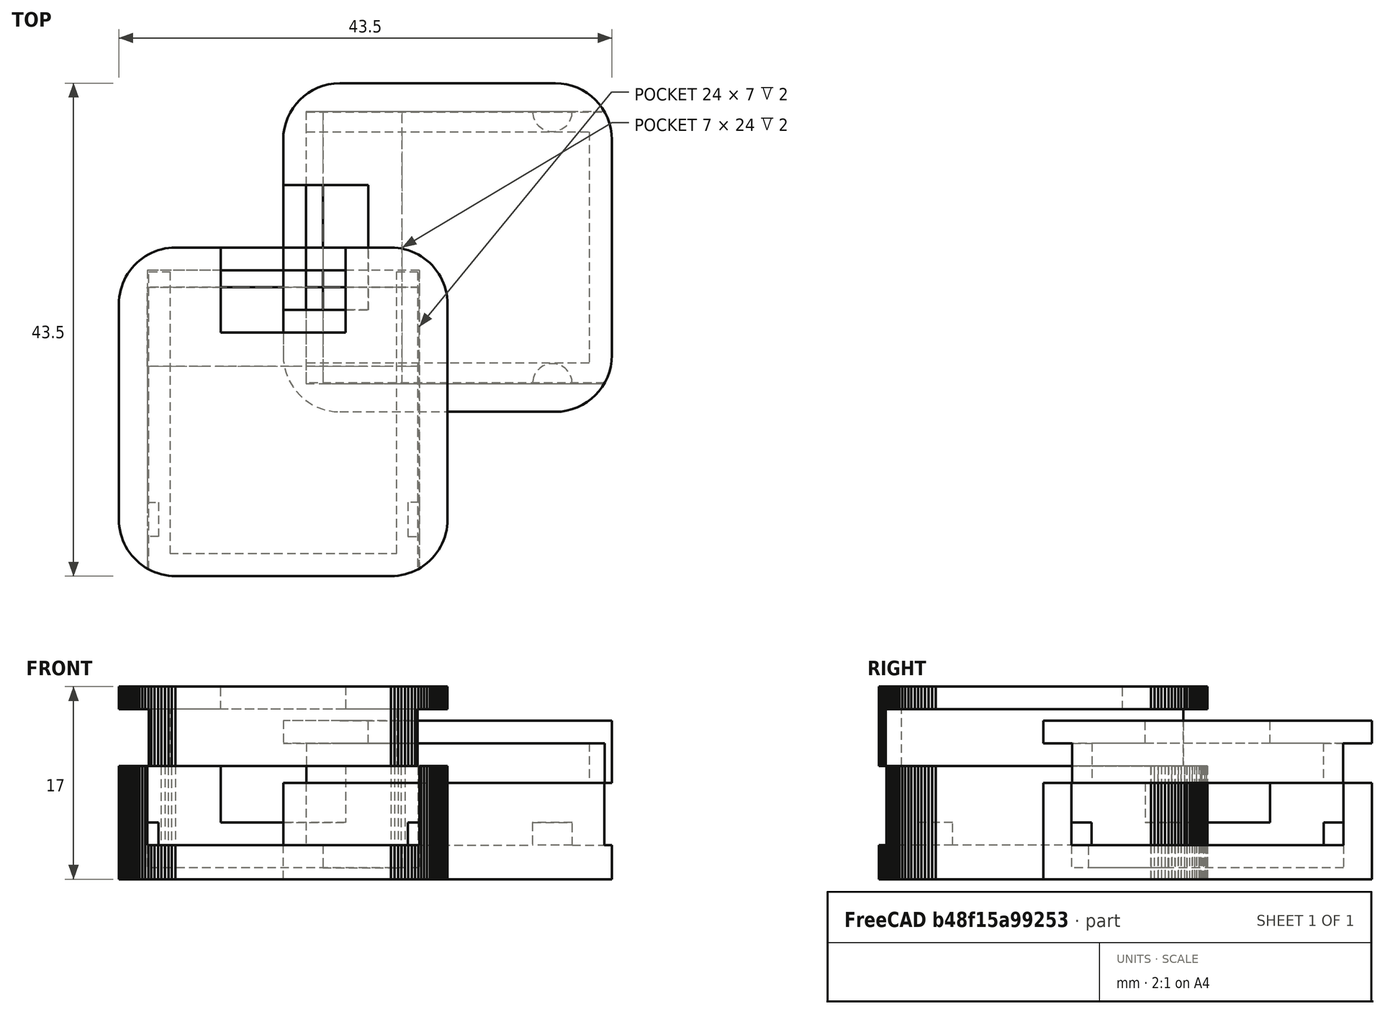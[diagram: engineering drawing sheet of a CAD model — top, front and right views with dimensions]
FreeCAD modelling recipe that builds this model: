
FCSTD DOCUMENT  (FreeCAD 1.0R39109 (Git))
Label: peepMoistureSensor
License: All rights reserved
LicenseURL: https://en.wikipedia.org/wiki/All_rights_reserved
objects: Sketcher::SketchObject×10, PartDesign::Pocket×6, PartDesign::Pad×4, Part::Feature×4, Mesh::Feature×2, Part::Refine×2, PartDesign::Body×2, Spreadsheet::Sheet×1
note: 58 computed .brp shape members not serialized (recipe doc carries the construction recipe); baked Part::Feature solids carry a one-line shape summary decoded from their .brp

FEATURE [Sketcher::SketchObject] Sketch
  ArcFitTolerance = 1e-06
  AttachmentSupport = -> [XY_Plane]
  FullyConstrained = true
  MakeInternals = false
  MapMode = 5
  expr: Constraints[10] = <<Parameters>>.baseHeight
  expr: Constraints[9] = <<Parameters>>.baseWidth
  sketch-geometry (4):
    g0: LineSegment StartX=0 StartY=0 StartZ=0 EndX=29 EndY=0 EndZ=0
    g1: LineSegment StartX=29 StartY=0 StartZ=0 EndX=29 EndY=29 EndZ=0
    g2: LineSegment StartX=29 StartY=29 StartZ=0 EndX=0 EndY=29 EndZ=0
    g3: LineSegment StartX=0 StartY=29 StartZ=0 EndX=0 EndY=0 EndZ=0
  constraints (11):
    c: Coincident(g0,g1)
    c: Coincident(g1,g2)
    c: Coincident(g2,g3)
    c: Coincident(g3,g0)
    c: Horizontal(g0)
    c: Horizontal(g2)
    c: Vertical(g1)
    c: Vertical(g3)
    c: Coincident(g0,g-1)
    c: DistanceX(g2,g2) = 29
    c: DistanceY(g1,g1) = 29
FEATURE [PartDesign::Pad] Pad
  Direction = (0,0,1)
  Length = 8.5
  Length2 = 10
  Profile = -> Sketch
  ReferenceAxis = -> Sketch [N_Axis]
  Refine = true
  Suppressed = false
  Type = 0
  expr: Length = <<Parameters>>.baseDepth
FEATURE [Spreadsheet::Sheet] Spreadsheet  label="Parameters"
  cells = B1='height; C1='width; D1='depth; E1='distance; F1='radius; A2='Base; B2(baseHeight)==29 mm; C2(baseWidth)==29 mm; D2(baseDepth)==wholePartDepth - frontDepth; A3='Cover; B3(coverHeight)==baseHeight; C3(coverWidth)==baseWidth; D3(coverDepth)==frontDepth + coverWallDepth; A4='Sensor; B4(sensorHeight)==24 mm; C4(sensorWidth)==27 mm; D4(sensorDepth)==2 mm; A5='Sensor pins; B5(sensorPinsHeight)==sensorHeight; C5(sensorPinsWidth)==7 mm; D5(sensorPinsDepth)==2 mm; A6='Sensor Holder distance from sensor edge; E6(sensorHolderDistance)==3.5 mm; A7='Sensor Holder; D7(sensorHolderDepth)==sensorDepth; F7(sensorHolderRadius)==1.75 mm; A8='Connector; B8(connectorHeight)==11 mm; C8(connectorWidth)==7.5 mm; D8(connectorDepth)==baseDepth - backDepth - connectorDistance; E8(connectorDistance)==2 mm; A9='Back; D9(backDepth)==3 mm; A10='Front; D10(frontDepth)==2 mm; A11='Cover wall; B11(coverWallHeight)=1.75; C11(coverWallWidth)==2 mm; D11(coverWallDepth)==baseDepth - backDepth - sensorDepth; A12='Pins distance from sensor connector edge; E12(pinsDistance)==1.5 mm; A13='Whole part decor round radius; F13(decorRoundRadius)==5 mm; A16='Thickness; A17='Whole part; D17(wholePartDepth)==10.5 mm; A18='Space between; D18(space)==0.05 mm
FEATURE [Mesh::Feature] Capacitive_Soil_Moisture_Sensor_v1_2_Lower  label="Capacitive_Soil_Moisture_Sensor_v1.2_Lower"
FEATURE [Part::Feature] Capacitive_Soil_Moisture_Sensor_v1_2_Lower001
  shape: bbox 29 x 29 x 10 mm, 492 faces, 0 solids (baked)
FEATURE [Part::Feature] Capacitive_Soil_Moisture_Sensor_v1_2_Lower001_solid  label="Capacitive_Soil_Moisture_Sensor_v1_2_Lower001 (Solid)"
  shape: bbox 29 x 29 x 10 mm, 492 faces (baked)
FEATURE [Part::Refine] Capacitive_Soil_Moisture_Sensor_v1_2_Lower001_solid001  label="Capacitive_Soil_Moisture_Sensor_v1_2_Lower001 (Solid)001"
  Source = -> Capacitive_Soil_Moisture_Sensor_v1_2_Lower001_solid
FEATURE [Sketcher::SketchObject] Sketch001
  ArcFitTolerance = 1e-06
  AttachmentSupport = -> [Pad]
  ExternalGeometry = -> [Pad]
  FullyConstrained = true
  MakeInternals = false
  MapMode = 5
  Placement = pos=(0,0,8.5) rot=(0,0,1;0rad)
  expr: Constraints[10] = <<Parameters>>.sensorWidth
  expr: Constraints[9] = <<Parameters>>.sensorHeight
  sketch-geometry (5):
    g0: GeomPoint X=29 Y=14.5 Z=0
    g1: LineSegment StartX=29 StartY=26.5 StartZ=0 EndX=2 EndY=26.5 EndZ=0
    g2: LineSegment StartX=2 StartY=26.5 StartZ=0 EndX=2 EndY=2.5 EndZ=0
    g3: LineSegment StartX=2 StartY=2.5 StartZ=0 EndX=29 EndY=2.5 EndZ=0
    g4: LineSegment StartX=29 StartY=2.5 StartZ=0 EndX=29 EndY=26.5 EndZ=0
  constraints (12):
    c: Coincident(g1,g2)
    c: Coincident(g2,g3)
    c: Coincident(g3,g4)
    c: Coincident(g4,g1)
    c: Horizontal(g1)
    c: Horizontal(g3)
    c: Vertical(g2)
    c: Vertical(g4)
    c: Symmetric(g1,g3,g0)
    c: DistanceY(g4,g4) = 24
    c: DistanceX(g1,g1) = 27
    c: Symmetric(g-4,g-6,g0)
FEATURE [PartDesign::Pocket] Pocket
  BaseFeature = -> Pad
  Direction = (0,0,-1)
  Length = 5.5
  Length2 = 5
  Profile = -> Sketch001
  ReferenceAxis = -> Sketch001 [N_Axis]
  Refine = true
  Suppressed = false
  Type = 0
  expr: Length = <<Parameters>>.baseDepth - <<Parameters>>.backDepth
FEATURE [Sketcher::SketchObject] Sketch002
  ArcFitTolerance = 1e-06
  AttachmentSupport = -> [Pocket]
  ExternalGeometry = -> [Pocket]
  FullyConstrained = true
  MakeInternals = false
  MapMode = 5
  Placement = pos=(0,0,3) rot=(0,0,1;0rad)
  expr: Constraints[10] = <<Parameters>>.pinsDistance
  expr: Constraints[11] = <<Parameters>>.sensorPinsWidth
  sketch-geometry (4):
    g0: LineSegment StartX=3.5 StartY=2.5 StartZ=0 EndX=10.5 EndY=2.5 EndZ=0
    g1: LineSegment StartX=10.5 StartY=2.5 StartZ=0 EndX=10.5 EndY=26.5 EndZ=0
    g2: LineSegment StartX=10.5 StartY=26.5 StartZ=0 EndX=3.5 EndY=26.5 EndZ=0
    g3: LineSegment StartX=3.5 StartY=26.5 StartZ=0 EndX=3.5 EndY=2.5 EndZ=0
  constraints (12):
    c: Coincident(g0,g1)
    c: Coincident(g1,g2)
    c: Coincident(g2,g3)
    c: Coincident(g3,g0)
    c: Horizontal(g0)
    c: Horizontal(g2)
    c: Vertical(g1)
    c: Vertical(g3)
    c: PointOnObject(g0,g-5)
    c: PointOnObject(g1,g-4)
    c: DistanceX(g-4,g2) = 1.5
    c: DistanceX(g2,g2) = 7
FEATURE [PartDesign::Pocket] Pocket001
  BaseFeature = -> Pocket
  Direction = (0,0,-1)
  Length = 2
  Length2 = 5
  Profile = -> Sketch002
  ReferenceAxis = -> Sketch002 [N_Axis]
  Refine = true
  Suppressed = false
  Type = 0
  expr: Length = <<Parameters>>.sensorPinsDepth
FEATURE [Sketcher::SketchObject] Sketch003
  ArcFitTolerance = 1e-06
  AttachmentSupport = -> [Pocket001]
  ExternalGeometry = -> [Pocket001]
  FullyConstrained = true
  MakeInternals = false
  MapMode = 5
  Placement = pos=(0,0,3) rot=(0,0,1;0rad)
  expr: Constraints[1] = <<Parameters>>.sensorHolderRadius
  expr: Constraints[2] = <<Parameters>>.sensorHolderDistance + <<Parameters>>.sensorHolderRadius
  expr: Constraints[5] = <<Parameters>>.sensorHolderRadius
  expr: Constraints[7] = <<Parameters>>.sensorHolderDistance + <<Parameters>>.sensorHolderRadius
  sketch-geometry (3):
    g0: Circle CenterX=23.75 CenterY=2.5 CenterZ=0 NormalX=0 NormalY=0 NormalZ=1 AngleXU=0 Radius=1.75
    g1: LineSegment [constr] StartX=10.5 StartY=14.5 StartZ=0 EndX=29 EndY=14.5 EndZ=0
    g2: Circle CenterX=23.75 CenterY=26.5 CenterZ=0 NormalX=0 NormalY=0 NormalZ=1 AngleXU=0 Radius=1.75
  constraints (8):
    c: PointOnObject(g0,g-5)
    c: Radius(g0) = 1.75
    c: DistanceX(g0,g-5) = 5.25
    c: Symmetric(g-4,g-5,g1)
    c: Symmetric(g-6,g-6,g1)
    c: Radius(g2) = 1.75
    c: PointOnObject(g2,g-3)
    c: DistanceX(g2,g-4) = 5.25
FEATURE [PartDesign::Pad] Pad001
  BaseFeature = -> Pocket001
  Direction = (0,0,1)
  Length = 2
  Length2 = 10
  Profile = -> Sketch003
  ReferenceAxis = -> Sketch003 [N_Axis]
  Refine = true
  Suppressed = false
  Type = 0
  expr: Length = <<Parameters>>.sensorHolderDepth
FEATURE [Sketcher::SketchObject] Sketch004
  ArcFitTolerance = 1e-06
  AttachmentSupport = -> [Pad001]
  ExternalGeometry = -> [Pad001]
  FullyConstrained = true
  MakeInternals = false
  MapMode = 5
  Placement = pos=(0,0,8.5) rot=(0,0,1;0rad)
  expr: Constraints[11] = <<Parameters>>.connectorHeight
  sketch-geometry (5):
    g0: LineSegment StartX=0 StartY=20 StartZ=0 EndX=0 EndY=9 EndZ=0
    g1: LineSegment StartX=0 StartY=9 StartZ=0 EndX=2 EndY=9 EndZ=0
    g2: LineSegment StartX=2 StartY=9 StartZ=0 EndX=2 EndY=20 EndZ=0
    g3: LineSegment StartX=2 StartY=20 StartZ=0 EndX=0 EndY=20 EndZ=0
    g4: GeomPoint X=0 Y=14.5 Z=0
  constraints (12):
    c: Coincident(g0,g1)
    c: Coincident(g1,g2)
    c: Coincident(g2,g3)
    c: Coincident(g3,g0)
    c: Vertical(g0)
    c: Vertical(g2)
    c: Horizontal(g1)
    c: Horizontal(g3)
    c: PointOnObject(g1,g-4)
    c: Symmetric(g0,g0,g4)
    c: Symmetric(g-6,g-1,g4)
    c: DistanceY(g2,g2) = 11
FEATURE [PartDesign::Pocket] Pocket002
  BaseFeature = -> Pad001
  Direction = (0,0,-1)
  Length = 3.5
  Length2 = 5
  Profile = -> Sketch004
  ReferenceAxis = -> Sketch004 [N_Axis]
  Refine = true
  Suppressed = false
  Type = 0
  expr: Length = <<Parameters>>.connectorDepth
FEATURE [Sketcher::SketchObject] Sketch005
  ArcFitTolerance = 1e-06
  AttachmentSupport = -> [Pocket002]
  ExternalGeometry = -> [Pocket002]
  FullyConstrained = true
  MakeInternals = false
  MapMode = 5
  Placement = pos=(0,0,0) rot=(1,0,0;3.14159rad)
  expr: Constraints[1] = <<Parameters>>.decorRoundRadius
  expr: Constraints[22] = <<Parameters>>.decorRoundRadius
  expr: Constraints[37] = <<Parameters>>.decorRoundRadius
  expr: Constraints[38] = <<Parameters>>.decorRoundRadius
  expr: Constraints[8] = <<Parameters>>.decorRoundRadius
  sketch-geometry (17):
    g0: ArcOfCircle CenterX=5 CenterY=-5 CenterZ=0 NormalX=0 NormalY=0 NormalZ=1 AngleXU=0 Radius=5 StartAngle=1.5708 EndAngle=3.14159
    g1: GeomPoint [constr] X=3.9941e-12 Y=-2.31e-14 Z=0
    g2: LineSegment StartX=3.9941e-12 StartY=-2.31e-14 StartZ=0 EndX=3.9941e-12 EndY=-5 EndZ=0
    g3: LineSegment StartX=3.9941e-12 StartY=-2.31e-14 StartZ=0 EndX=5 EndY=-2.31e-14 EndZ=0
    g4: GeomPoint X=0 Y=-14.5 Z=0
    g5: GeomPoint X=14.5 Y=0 Z=0
    g6: LineSegment [constr] StartX=0 StartY=-14.5 StartZ=0 EndX=29 EndY=-14.5 EndZ=0
    g7: LineSegment [constr] StartX=14.5 StartY=0 StartZ=0 EndX=14.5 EndY=-29 EndZ=0
    g8: ArcOfCircle CenterX=5 CenterY=-24 CenterZ=0 NormalX=0 NormalY=0 NormalZ=1 AngleXU=0 Radius=5 StartAngle=3.14159 EndAngle=4.71239
    g9: LineSegment StartX=0 StartY=-29 StartZ=0 EndX=0 EndY=-24 EndZ=0
    g10: LineSegment StartX=0 StartY=-29 StartZ=0 EndX=5 EndY=-29 EndZ=0
    g11: ArcOfCircle CenterX=24 CenterY=-5 CenterZ=0 NormalX=0 NormalY=0 NormalZ=1 AngleXU=0 Radius=5 StartAngle=0 EndAngle=1.5708
    g12: LineSegment StartX=29 StartY=0 StartZ=0 EndX=24 EndY=0 EndZ=0
    g13: LineSegment StartX=29 StartY=0 StartZ=0 EndX=29 EndY=-5 EndZ=0
    g14: ArcOfCircle CenterX=24 CenterY=-24 CenterZ=0 NormalX=0 NormalY=0 NormalZ=1 AngleXU=0 Radius=5 StartAngle=4.71239 EndAngle=6.28319
    g15: LineSegment StartX=29 StartY=-29 StartZ=0 EndX=24 EndY=-29 EndZ=0
    g16: LineSegment StartX=29 StartY=-29 StartZ=0 EndX=29 EndY=-24 EndZ=0
  constraints (43):
    c: Coincident(g1,g-1)
    c: Radius(g0) = 5
    c: Coincident(g2,g1)
    c: Tangent(g2,g0) = -1.5708
    c: Vertical(g2)
    c: Coincident(g3,g1)
    c: Coincident(g3,g0)
    c: Horizontal(g3)
    c: DistanceX(g1,g0) = 5
    c: Symmetric(g-4,g1,g5)
    c: Symmetric(g-3,g1,g4)
    c: Coincident(g6,g4)
    c: PointOnObject(g6,g-6)
    c: Coincident(g7,g5)
    c: PointOnObject(g7,g-5)
    c: Horizontal(g6)
    c: Vertical(g7)
    c: Radius(g8) = 5
    c: Tangent(g9,g8) = 1.5708
    c: Vertical(g9)
    c: Coincident(g10,g8)
    c: Horizontal(g10)
    c: DistanceX(g10,g10) = 5
    c: PointOnObject(g8,g-5)
    c: PointOnObject(g8,g-3)
    c: Coincident(g9,g10)
    c: Radius(g11) = 5
    c: Tangent(g13,g11) = 1.5708
    c: Vertical(g13)
    c: Coincident(g12,g11)
    c: Horizontal(g12)
    c: Radius(g14) = 5
    c: Tangent(g16,g14) = -1.5708
    c: Vertical(g16)
    c: Coincident(g15,g14)
    c: Horizontal(g15)
    c: Coincident(g16,g15)
    c: DistanceX(g15,g15) = 5
    c: DistanceX(g12,g12) = 5
    c: PointOnObject(g14,g-5)
    c: PointOnObject(g14,g-6)
    c: Coincident(g-6,g13)
    c: Coincident(g12,g13)
FEATURE [PartDesign::Pocket] Pocket003
  BaseFeature = -> Pocket002
  Direction = (0,0,1)
  Length = 5
  Length2 = 5
  Profile = -> Sketch005
  ReferenceAxis = -> Sketch005 [N_Axis]
  Refine = true
  Suppressed = false
  Type = 1
FEATURE [PartDesign::Body] Body  label="Base"
  AllowCompound = false
  Group = -> [Sketch,Pad,Sketch001,Pocket,Sketch002,Pocket001,Sketch003,Pad001,Sketch004,Pocket002,Sketch005,Pocket003]
  Origin = -> Origin
  Tip = -> Pocket003
FEATURE [Sketcher::SketchObject] Sketch006
  ArcFitTolerance = 1e-06
  AttachmentSupport = -> [XY_Plane001]
  FullyConstrained = true
  MakeInternals = false
  MapMode = 5
  expr: Constraints[10] = <<Parameters>>.coverWidth
  expr: Constraints[11] = <<Parameters>>.coverHeight
  sketch-geometry (4):
    g0: LineSegment StartX=0 StartY=29 StartZ=0 EndX=0 EndY=0 EndZ=0
    g1: LineSegment StartX=0 StartY=0 StartZ=0 EndX=29 EndY=0 EndZ=0
    g2: LineSegment StartX=29 StartY=0 StartZ=0 EndX=29 EndY=29 EndZ=0
    g3: LineSegment StartX=29 StartY=29 StartZ=0 EndX=0 EndY=29 EndZ=0
  constraints (12):
    c: Coincident(g0,g1)
    c: Coincident(g1,g2)
    c: Coincident(g2,g3)
    c: Coincident(g3,g0)
    c: Vertical(g0)
    c: Vertical(g2)
    c: Horizontal(g1)
    c: Horizontal(g3)
    c: PointOnObject(g0,g-2)
    c: PointOnObject(g1,g-1)
    c: DistanceX(g3,g3) = 29
    c: DistanceY(g2,g2) = 29
FEATURE [PartDesign::Pad] Pad002
  Direction = (0,0,1)
  Length = 2
  Length2 = 10
  Profile = -> Sketch006
  ReferenceAxis = -> Sketch006 [N_Axis]
  Refine = true
  Reversed = true
  Suppressed = false
  Type = 0
  expr: Length = <<Parameters>>.frontDepth
FEATURE [Mesh::Feature] Capacitive_Soil_Moisture_Sensor_v1_2_Upper  label="Capacitive_Soil_Moisture_Sensor_v1.2_Upper"
FEATURE [Part::Feature] Capacitive_Soil_Moisture_Sensor_v1_2_Upper001
  shape: bbox 29 x 29 x 7 mm, 476 faces, 0 solids (baked)
FEATURE [Part::Feature] Capacitive_Soil_Moisture_Sensor_v1_2_Upper001_solid  label="Capacitive_Soil_Moisture_Sensor_v1_2_Upper001 (Solid)"
  shape: bbox 29 x 29 x 7 mm, 476 faces (baked)
FEATURE [Part::Refine] Capacitive_Soil_Moisture_Sensor_v1_2_Upper001_solid001  label="Capacitive_Soil_Moisture_Sensor_v1_2_Upper001 (Solid)001"
  Source = -> Capacitive_Soil_Moisture_Sensor_v1_2_Upper001_solid
FEATURE [Sketcher::SketchObject] Sketch007
  ArcFitTolerance = 1e-06
  AttachmentSupport = -> [Pad002]
  ExternalGeometry = -> [Pad002]
  FullyConstrained = true
  MakeInternals = false
  MapMode = 5
  Placement = pos=(0,0,-2) rot=(1,0,0;3.14159rad)
  expr: Constraints[18] = <<Parameters>>.sensorHeight - <<Parameters>>.space * 2
  expr: Constraints[19] = <<Parameters>>.coverWallWidth
  expr: Constraints[20] = <<Parameters>>.coverWallHeight
  expr: Constraints[21] = <<Parameters>>.coverWallHeight
  expr: Constraints[22] = <<Parameters>>.sensorWidth - <<Parameters>>.space
  expr: Constraints[23] = <<Parameters>>.sensorWidth - <<Parameters>>.space
  sketch-geometry (9):
    g0: GeomPoint X=29 Y=-14.5 Z=0
    g1: LineSegment StartX=2.05 StartY=-26.45 StartZ=0 EndX=29 EndY=-26.45 EndZ=0
    g2: LineSegment StartX=29 StartY=-26.45 StartZ=0 EndX=29 EndY=-2.55 EndZ=0
    g3: LineSegment StartX=29 StartY=-2.55 StartZ=0 EndX=2.05 EndY=-2.55 EndZ=0
    g4: LineSegment StartX=2.05 StartY=-24.7 StartZ=0 EndX=27 EndY=-24.7 EndZ=0
    g5: LineSegment StartX=27 StartY=-24.7 StartZ=0 EndX=27 EndY=-4.3 EndZ=0
    g6: LineSegment StartX=27 StartY=-4.3 StartZ=0 EndX=2.05 EndY=-4.3 EndZ=0
    g7: LineSegment StartX=2.05 StartY=-2.55 StartZ=0 EndX=2.05 EndY=-4.3 EndZ=0
    g8: LineSegment StartX=2.05 StartY=-24.7 StartZ=0 EndX=2.05 EndY=-26.45 EndZ=0
  constraints (24):
    c: Symmetric(g-3,g-3,g0)
    c: Coincident(g1,g2)
    c: Coincident(g2,g3)
    c: Vertical(g2)
    c: Horizontal(g1)
    c: Horizontal(g3)
    c: Coincident(g4,g5)
    c: Coincident(g5,g6)
    c: Vertical(g5)
    c: Horizontal(g4)
    c: Horizontal(g6)
    c: Coincident(g7,g3)
    c: Coincident(g7,g6)
    c: Vertical(g7)
    c: Coincident(g8,g4)
    c: Coincident(g8,g1)
    c: Vertical(g8)
    c: Symmetric(g2,g1,g0)
    c: DistanceY(g1,g2) = 23.9
    c: DistanceX(g5,g2) = 2
    c: DistanceY(g1,g4) = 1.75
    c: DistanceY(g6,g3) = 1.75
    c: DistanceX(g3,g2) = 26.95
    c: DistanceX(g1,g1) = 26.95
FEATURE [PartDesign::Pad] Pad003
  BaseFeature = -> Pad002
  Direction = (0,0,-1)
  Length = 3.5
  Length2 = 10
  Profile = -> Sketch007
  ReferenceAxis = -> Sketch007 [N_Axis]
  Refine = true
  Suppressed = false
  Type = 0
  expr: Length = <<Parameters>>.coverWallDepth
FEATURE [Sketcher::SketchObject] Sketch008
  ArcFitTolerance = 1e-06
  AttachmentSupport = -> [Pad003]
  ExternalGeometry = -> [Pad003]
  FullyConstrained = true
  MakeInternals = false
  MapMode = 5
  Placement = pos=(0,0,-2) rot=(1,0,0;3.14159rad)
  expr: Constraints[10] = <<Parameters>>.connectorHeight
  expr: Constraints[9] = <<Parameters>>.connectorWidth
  sketch-geometry (5):
    g0: GeomPoint X=0 Y=-14.5 Z=0
    g1: LineSegment StartX=0 StartY=-9 StartZ=0 EndX=0 EndY=-20 EndZ=0
    g2: LineSegment StartX=0 StartY=-20 StartZ=0 EndX=7.5 EndY=-20 EndZ=0
    g3: LineSegment StartX=7.5 StartY=-20 StartZ=0 EndX=7.5 EndY=-9 EndZ=0
    g4: LineSegment StartX=7.5 StartY=-9 StartZ=0 EndX=0 EndY=-9 EndZ=0
  constraints (12):
    c: Symmetric(g-3,g-3,g0)
    c: Coincident(g1,g2)
    c: Coincident(g2,g3)
    c: Coincident(g3,g4)
    c: Coincident(g4,g1)
    c: Vertical(g1)
    c: Vertical(g3)
    c: Horizontal(g2)
    c: Horizontal(g4)
    c: DistanceX(g4,g4) = 7.5
    c: DistanceY(g3,g3) = 11
    c: Symmetric(g1,g1,g0)
FEATURE [PartDesign::Pocket] Pocket004
  BaseFeature = -> Pad003
  Direction = (0,0,1)
  Length = 5
  Length2 = 5
  Profile = -> Sketch008
  ReferenceAxis = -> Sketch008 [N_Axis]
  Refine = true
  Suppressed = false
  Type = 1
FEATURE [Sketcher::SketchObject] Sketch009
  ArcFitTolerance = 1e-06
  AttachmentSupport = -> [Pocket004]
  ExternalGeometry = -> [Pocket004]
  FullyConstrained = true
  MakeInternals = false
  MapMode = 5
  expr: Constraints[24] = <<Parameters>>.decorRoundRadius
  expr: Constraints[40] = <<Parameters>>.decorRoundRadius
  expr: Constraints[41] = <<Parameters>>.decorRoundRadius
  expr: Constraints[7] = <<Parameters>>.decorRoundRadius
  sketch-geometry (20):
    g0: ArcOfCircle CenterX=5 CenterY=24 CenterZ=0 NormalX=0 NormalY=0 NormalZ=1 AngleXU=0 Radius=5 StartAngle=1.5708 EndAngle=3.14159
    g1: GeomPoint [constr] X=6.2e-15 Y=29 Z=0
    g2: LineSegment StartX=6.2e-15 StartY=29 StartZ=0 EndX=6.2e-15 EndY=24 EndZ=0
    g3: LineSegment StartX=6.2e-15 StartY=29 StartZ=0 EndX=5 EndY=29 EndZ=0
    g4: GeomPoint X=14.5 Y=29 Z=0
    g5: GeomPoint X=29 Y=14.5 Z=0
    g6: GeomPoint X=7.5 Y=14.5 Z=0
    g7: LineSegment [constr] StartX=7.5 StartY=14.5 StartZ=0 EndX=29 EndY=14.5 EndZ=0
    g8: GeomPoint X=14.5 Y=0 Z=0
    g9: LineSegment [constr] StartX=14.5 StartY=29 StartZ=0 EndX=14.5 EndY=0 EndZ=0
    g10: LineSegment StartX=29 StartY=29 StartZ=0 EndX=29 EndY=24 EndZ=0
    g11: ArcOfCircle CenterX=24 CenterY=24 CenterZ=0 NormalX=0 NormalY=0 NormalZ=1 AngleXU=0 Radius=5 StartAngle=1e-16 EndAngle=1.5708
    g12: LineSegment StartX=29 StartY=29 StartZ=0 EndX=24 EndY=29 EndZ=0
    g13: LineSegment StartX=29 StartY=0 StartZ=0 EndX=24 EndY=0 EndZ=0
    g14: LineSegment StartX=29 StartY=0 StartZ=0 EndX=29 EndY=5 EndZ=0
    g15: ArcOfCircle CenterX=24 CenterY=5 CenterZ=0 NormalX=0 NormalY=0 NormalZ=1 AngleXU=0 Radius=5 StartAngle=4.71239 EndAngle=6.28319
    g16: LineSegment StartX=0 StartY=0 StartZ=0 EndX=5 EndY=1.1058e-12 EndZ=0
    g17: ArcOfCircle CenterX=5 CenterY=5 CenterZ=0 NormalX=0 NormalY=0 NormalZ=1 AngleXU=0 Radius=5 StartAngle=3.14159 EndAngle=4.71239
    g18: LineSegment StartX=0 StartY=0 StartZ=0 EndX=8e-15 EndY=5 EndZ=0
    g19: GeomPoint [constr] X=0 Y=0 Z=0
  constraints (42):
    c: Coincident(g1,g-7)
    c: Coincident(g2,g1)
    c: Coincident(g2,g0)
    c: Vertical(g2)
    c: Coincident(g3,g1)
    c: Tangent(g3,g0) = 1.5708
    c: Horizontal(g3)
    c: DistanceX(g3,g3) = 5
    c: Equal(g2,g3)
    c: Symmetric(g-7,g-7,g4)
    c: Symmetric(g-6,g-6,g5)
    c: Symmetric(g-8,g-8,g6)
    c: Coincident(g7,g6)
    c: Coincident(g7,g5)
    c: Symmetric(g-5,g-5,g8)
    c: Coincident(g9,g4)
    c: Coincident(g9,g8)
    c: Coincident(g10,g11)
    c: Tangent(g12,g11) = -1.5708
    c: Equal(g10,g12)
    c: PointOnObject(g11,g-7)
    c: PointOnObject(g10,g-6)
    c: Coincident(g12,g10)
    c: Coincident(g-7,g10)
    c: DistanceX(g12,g12) = 5
    c: Coincident(g18,g19)
    c: Coincident(g18,g17)
    c: Coincident(g16,g19)
    c: Tangent(g16,g17) = -1.5708
    c: Equal(g18,g16)
    c: Coincident(g14,g15)
    c: Tangent(g13,g15) = 1.5708
    c: Equal(g14,g13)
    c: Coincident(g13,g14)
    c: PointOnObject(g13,g-5)
    c: PointOnObject(g14,g-6)
    c: Coincident(g13,g-6)
    c: PointOnObject(g17,g-4)
    c: PointOnObject(g16,g-5)
    c: Coincident(g16,g-1)
    c: DistanceX(g13,g13) = 5
    c: DistanceX(g16,g16) = 5
FEATURE [PartDesign::Pocket] Pocket005
  BaseFeature = -> Pocket004
  Direction = (0,0,-1)
  Length = 5
  Length2 = 5
  Profile = -> Sketch009
  ReferenceAxis = -> Sketch009 [N_Axis]
  Refine = true
  Suppressed = false
  Type = 1
FEATURE [PartDesign::Body] Body001  label="Cover"
  AllowCompound = false
  Group = -> [Sketch006,Pad002,Sketch007,Pad003,Sketch008,Pocket004,Sketch009,Pocket005]
  Origin = -> Origin001
  Placement = pos=(0,0,14) rot=(0,0,1;0rad)
  Tip = -> Pocket005
  expr: .Placement.Base.z = <<Parameters>>.baseDepth + <<Parameters>>.coverDepth
